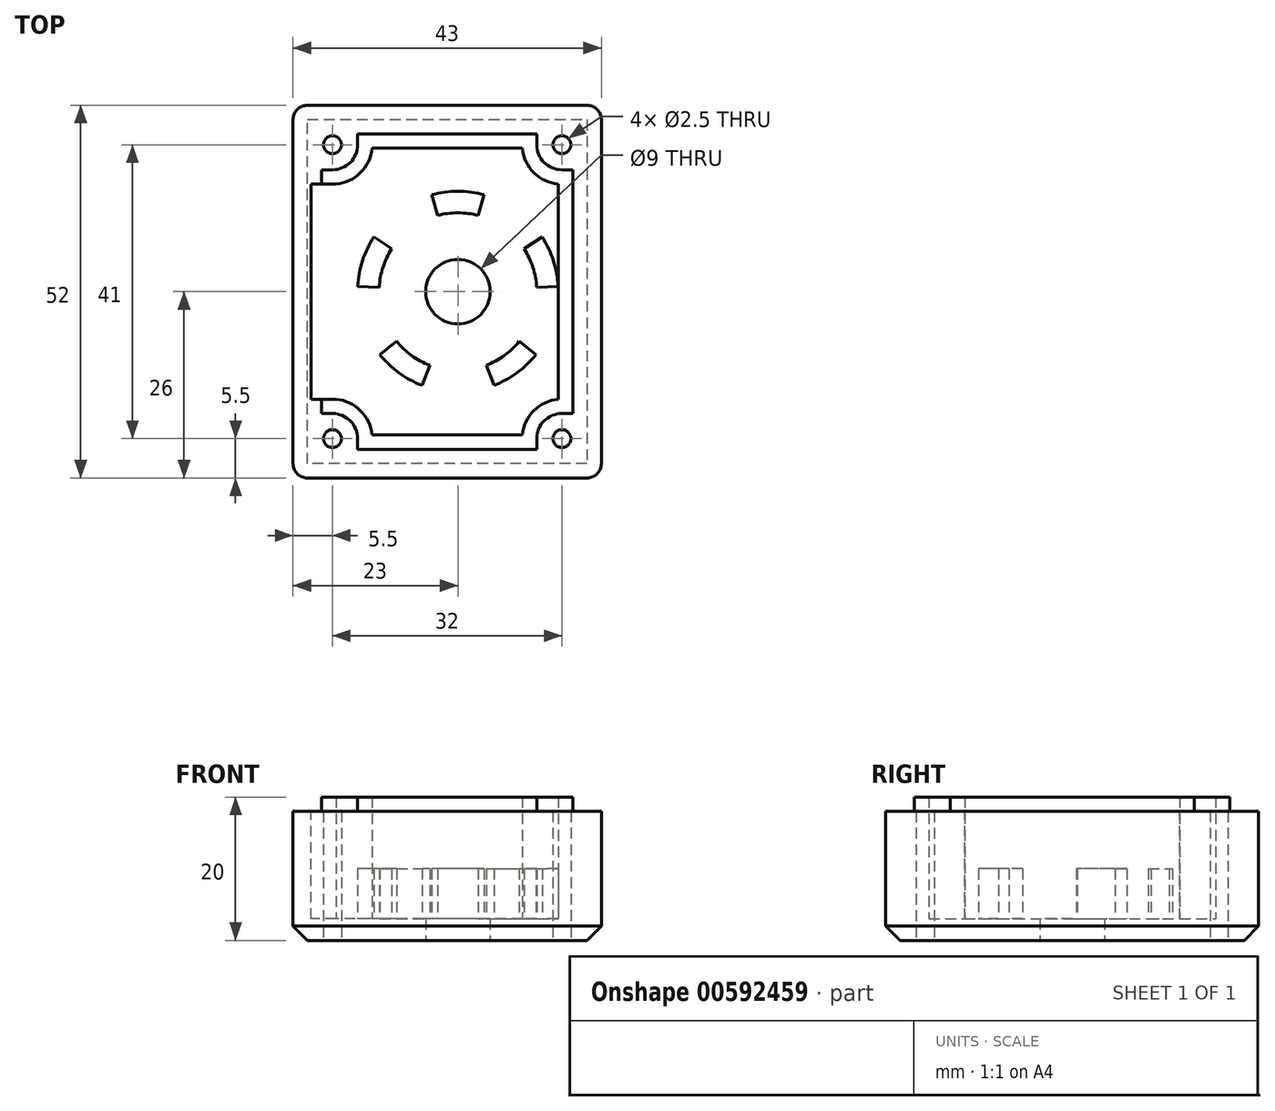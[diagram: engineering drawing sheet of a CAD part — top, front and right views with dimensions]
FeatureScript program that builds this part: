
annotation { "Feature Type Name" : "Feature", "Feature Type Description" : "" }
export const myFeature = defineFeature(function(context is Context, id is Id, definition is map)
    precondition{}
    {
        {
            var Q0;
            Q0=qCreatedBy(makeId("Top.planeOp"),FACE);
            var sketch = newSketch(context, id + "F0", { "sketchPlane" : qUnion([Q0])});
            skLineSegment(sketch, "E0.0", {"start": v(-18.64, 26) * mm, "end": v(20.36, 26) * mm});
            skArc(sketch, "E0.1", {"start": v(-18.64, 26) * mm, "mid": v(-20.05, 25.41) * mm, "end": v(-20.64, 24) * mm});
            skLineSegment(sketch, "E0.2", {"start": v(-20.64, 24) * mm, "end": v(-20.64, -24) * mm});
            skLineSegment(sketch, "E0.3", {"start": v(-17.64, 18) * mm, "end": v(-17.64, -18) * mm});
            skLineSegment(sketch, "E0.4", {"start": v(-15.14, 18) * mm, "end": v(-18.64, 18) * mm});
            skArc(sketch, "E0.5", {"start": v(-15.14, 18) * mm, "mid": v(-13.37, 18.73) * mm, "end": v(-12.64, 20.5) * mm});
            skLineSegment(sketch, "E0.6", {"start": v(-12.64, 20.5) * mm, "end": v(-12.64, 24) * mm});
            skLineSegment(sketch, "E0.7", {"start": v(14.36, 23) * mm, "end": v(-12.64, 23) * mm});
            skLineSegment(sketch, "E0.8", {"start": v(14.36, 20.5) * mm, "end": v(14.36, 24) * mm});
            skArc(sketch, "E0.9", {"start": v(14.36, 20.5) * mm, "mid": v(15.1, 18.73) * mm, "end": v(16.86, 18) * mm});
            skLineSegment(sketch, "E0.10", {"start": v(16.86, 18) * mm, "end": v(20.36, 18) * mm});
            skLineSegment(sketch, "E0.11", {"start": v(19.36, -18) * mm, "end": v(19.36, 18) * mm});
            skLineSegment(sketch, "E0.12", {"start": v(16.86, -18) * mm, "end": v(20.36, -18) * mm});
            skArc(sketch, "E0.13", {"start": v(16.86, -18) * mm, "mid": v(15.1, -18.73) * mm, "end": v(14.36, -20.5) * mm});
            skLineSegment(sketch, "E0.14", {"start": v(14.36, -20.5) * mm, "end": v(14.36, -24) * mm});
            skLineSegment(sketch, "E0.15", {"start": v(-12.64, -23) * mm, "end": v(14.36, -23) * mm});
            skLineSegment(sketch, "E0.16", {"start": v(-12.64, -24) * mm, "end": v(-12.64, -20.5) * mm});
            skArc(sketch, "E0.17", {"start": v(-12.64, -20.5) * mm, "mid": v(-13.37, -18.73) * mm, "end": v(-15.14, -18) * mm});
            skLineSegment(sketch, "E0.18", {"start": v(-15.14, -18) * mm, "end": v(-18.64, -18) * mm});
            skArc(sketch, "E0.20", {"start": v(-20.64, -24) * mm, "mid": v(-20.05, -25.41) * mm, "end": v(-18.64, -26) * mm});
            skLineSegment(sketch, "E0.21", {"start": v(-18.64, -26) * mm, "end": v(20.36, -26) * mm});
            skArc(sketch, "E0.22", {"start": v(20.36, -26) * mm, "mid": v(21.77, -25.41) * mm, "end": v(22.36, -24) * mm});
            skLineSegment(sketch, "E0.23", {"start": v(22.36, 24) * mm, "end": v(22.36, -24) * mm});
            skArc(sketch, "E0.24", {"start": v(22.36, 24) * mm, "mid": v(21.77, 25.41) * mm, "end": v(20.36, 26) * mm});
            skSolve(sketch);
        }
        {
            var Q0;
            Q0=qCreatedBy(makeId("Top.planeOp"),FACE);
            var sketch = newSketch(context, id + "F1", { "sketchPlane" : qUnion([Q0])});
            skLineSegment(sketch, "E1", {"start": v(-16.64, 17) * mm, "end": v(-16.64, -17) * mm});
            skLineSegment(sketch, "E2", {"start": v(-16.64, -17) * mm, "end": v(-15.14, -17) * mm});
            skLineSegment(sketch, "E3", {"start": v(-11.64, -20.5) * mm, "end": v(-11.64, -22) * mm});
            skLineSegment(sketch, "E4", {"start": v(-11.64, -22) * mm, "end": v(13.36, -22) * mm});
            skLineSegment(sketch, "E5", {"start": v(13.36, -22) * mm, "end": v(13.36, -20.5) * mm});
            skLineSegment(sketch, "E6", {"start": v(16.86, -17) * mm, "end": v(18.36, -17) * mm});
            skLineSegment(sketch, "E7", {"start": v(18.36, -17) * mm, "end": v(18.36, 17) * mm});
            skLineSegment(sketch, "E8", {"start": v(18.36, 17) * mm, "end": v(16.86, 17) * mm});
            skLineSegment(sketch, "E9", {"start": v(13.36, 20.5) * mm, "end": v(13.36, 22) * mm});
            skLineSegment(sketch, "E10", {"start": v(13.36, 22) * mm, "end": v(-11.64, 22) * mm});
            skLineSegment(sketch, "E11", {"start": v(-11.64, 22) * mm, "end": v(-11.64, 20.5) * mm});
            skLineSegment(sketch, "E12", {"start": v(-15.14, 17) * mm, "end": v(-16.64, 17) * mm});
            skArc(sketch, "E13", {"start": v(-15.14, 17) * mm, "mid": v(-12.67, 18.03) * mm, "end": v(-11.64, 20.5) * mm});
            skArc(sketch, "E14", {"start": v(13.36, 20.5) * mm, "mid": v(14.39, 18.03) * mm, "end": v(16.86, 17) * mm});
            skArc(sketch, "E15", {"start": v(16.86, -17) * mm, "mid": v(14.39, -18.03) * mm, "end": v(13.36, -20.5) * mm});
            skArc(sketch, "E16", {"start": v(-11.64, -20.5) * mm, "mid": v(-12.67, -18.03) * mm, "end": v(-15.14, -17) * mm});
            skSolve(sketch);
        }
        {
            var Q0;
            Q0=makeQuery(id+"F1.imprint","IMPRINT",FACE,{"disambiguationData":[TD([[makeQuery(id+"F1.imprint","IMPRINT",EDGE,{"derivedFrom":sQuery(id+"F1.wireOp",EDGE,"E1")}),1.0]])]});
            extrude(context, id + "F2", {"entities" : qUnion([Q0]), "depth" : 2 * mm, "offsetDistance" : 25 * mm});
        }
        {
            var Q0;
            Q0=makeQuery(id+"F0.imprint","IMPRINT",FACE,{"disambiguationData":[TD([[makeQuery(id+"F0.imprint","IMPRINT",EDGE,{"derivedFrom":sQuery(id+"F0.wireOp",EDGE,"E0.0")}),-1.0]])]});
            var Q1;
            {var subQ7=sQuery(id+"F0.wireOp",EDGE,"E0.3");Q1=makeQuery(id+"F0.imprint","IMPRINT",FACE,{"disambiguationData":[TD([[makeQuery(id+"F0.imprint","IMPRINT",EDGE,{"derivedFrom":subQ7}),1.0]])]});}
            extrude(context, id + "F3", {"entities" : qUnion([Q0, Q1]), "operationType" : NewBodyOperationType.ADD, "oppositeDirection" : true, "depth" : 3 * mm, "offsetDistance" : 25 * mm});
        }
        {
            var Q0;
            Q0=makeQuery(id+"F3.opExtrude","CAP_FACE",FACE,{"disambiguationData":[OSD([sQuery(id+"F0.wireOp",EDGE,"E0.0"),sQuery(id+"F0.wireOp",EDGE,"E0.1"),sQuery(id+"F0.wireOp",EDGE,"E0.2"),sQuery(id+"F0.wireOp",EDGE,"E0.20"),sQuery(id+"F0.wireOp",EDGE,"E0.21"),sQuery(id+"F0.wireOp",EDGE,"E0.22"),sQuery(id+"F0.wireOp",EDGE,"E0.23"),sQuery(id+"F0.wireOp",EDGE,"E0.24")])],"isStart":false});
            var sketch = newSketch(context, id + "F4", { "sketchPlane" : qUnion([Q0])});
            skCircle(sketch, "E17", {"center": v(2.36, 0) * mm, "radius": 4.5 * mm});
            skPoint(sketch, "E18", {"position": v(22.36, 0) * mm});
            skSolve(sketch);
        }
        {
            var Q0;
            Q0=makeQuery(id+"F4.imprint","IMPRINT",FACE,{"disambiguationData":[TD([[makeQuery(id+"F4.imprint","IMPRINT",EDGE,{"derivedFrom":sQuery(id+"F4.wireOp",EDGE,"E17")}),1.0]])]});
            extrude(context, id + "F5", {"entities" : qUnion([Q0]), "operationType" : NewBodyOperationType.REMOVE, "endBound" : BoundingType.UP_TO_NEXT, "oppositeDirection" : true, "depth" : 25 * mm, "offsetDistance" : 25 * mm});
        }
        {
            var Q0;
            Q0=makeQuery(id+"F3.opExtrude","CAP_FACE",FACE,{"disambiguationData":[OSD([sQuery(id+"F0.wireOp",EDGE,"E0.0"),sQuery(id+"F0.wireOp",EDGE,"E0.1"),sQuery(id+"F0.wireOp",EDGE,"E0.2"),sQuery(id+"F0.wireOp",EDGE,"E0.20"),sQuery(id+"F0.wireOp",EDGE,"E0.21"),sQuery(id+"F0.wireOp",EDGE,"E0.22"),sQuery(id+"F0.wireOp",EDGE,"E0.23"),sQuery(id+"F0.wireOp",EDGE,"E0.24")])],"isStart":false});
            var sketch = newSketch(context, id + "F6", { "sketchPlane" : qUnion([Q0])});
            skPoint(sketch, "E19", {"position": v(16.86, 20.5) * mm});
            skPoint(sketch, "E20", {"position": v(-15.14, -20.5) * mm});
            skPoint(sketch, "E21", {"position": v(-15.14, 20.5) * mm});
            skPoint(sketch, "E22", {"position": v(16.86, -20.5) * mm});
            skSolve(sketch);
        }
        {
            var Q0;
            Q0=sQuery(id+"F6.wireOp",VERTEX,"E21");
            var Q1;
            Q1=sQuery(id+"F6.wireOp",VERTEX,"E19");
            var Q2;
            Q2=sQuery(id+"F6.wireOp",VERTEX,"E22");
            var Q3;
            Q3=sQuery(id+"F6.wireOp",VERTEX,"E20");
            var Q4;
            Q4=makeQuery(id+"F2.opExtrude","SWEPT_BODY",BODY,{"disambiguationData":[OSD([sQuery(id+"F1.wireOp",EDGE,"E1"),sQuery(id+"F1.wireOp",EDGE,"E2"),sQuery(id+"F1.wireOp",EDGE,"E3"),sQuery(id+"F1.wireOp",EDGE,"E4"),sQuery(id+"F1.wireOp",EDGE,"E5"),sQuery(id+"F1.wireOp",EDGE,"E6"),sQuery(id+"F1.wireOp",EDGE,"E7"),sQuery(id+"F1.wireOp",EDGE,"E8"),sQuery(id+"F1.wireOp",EDGE,"E9"),sQuery(id+"F1.wireOp",EDGE,"E10"),sQuery(id+"F1.wireOp",EDGE,"E11"),sQuery(id+"F1.wireOp",EDGE,"E12"),sQuery(id+"F1.wireOp",EDGE,"E13"),sQuery(id+"F1.wireOp",EDGE,"E14"),sQuery(id+"F1.wireOp",EDGE,"E15"),sQuery(id+"F1.wireOp",EDGE,"E16")])]});
            hole(context, id + "F7", {"style" : HoleStyle.SIMPLE, "endStyle" : HoleEndStyle.THROUGH, "standardTappedOrClearance" : lookupTablePath({ "standard" : "ISO", "engagement" : "75%", "pitch" : "0.5 mm", "size" : "M3", "type" : "Tapped" }), "standardBlindInLast" : lookupTablePath({ "standard" : "ISO", "engagement" : "75%", "pitch" : "0.5 mm", "size" : "M3", "type" : "Tapped" }), "holeDiameter" : 2.5 * mm, "majorDiameter" : 3 * mm, "showTappedDepth" : true, "isTappedThrough" : true, "tappedDepth" : 8.5 * mm, "tapClearance" : 3, "startFromSketch" : true, "locations" : qUnion([Q0, Q1, Q2, Q3]), "scope" : qUnion([Q4])});
        }
        {
            var Q0;
            Q0=makeQuery(id+"F2.opExtrude","CAP_FACE",FACE,{"disambiguationData":[OSD([sQuery(id+"F1.wireOp",EDGE,"E1"),sQuery(id+"F1.wireOp",EDGE,"E2"),sQuery(id+"F1.wireOp",EDGE,"E3"),sQuery(id+"F1.wireOp",EDGE,"E4"),sQuery(id+"F1.wireOp",EDGE,"E5"),sQuery(id+"F1.wireOp",EDGE,"E6"),sQuery(id+"F1.wireOp",EDGE,"E7"),sQuery(id+"F1.wireOp",EDGE,"E8"),sQuery(id+"F1.wireOp",EDGE,"E9"),sQuery(id+"F1.wireOp",EDGE,"E10"),sQuery(id+"F1.wireOp",EDGE,"E11"),sQuery(id+"F1.wireOp",EDGE,"E12"),sQuery(id+"F1.wireOp",EDGE,"E13"),sQuery(id+"F1.wireOp",EDGE,"E14"),sQuery(id+"F1.wireOp",EDGE,"E15"),sQuery(id+"F1.wireOp",EDGE,"E16")])],"isStart":false});
            var sketch = newSketch(context, id + "F8", { "sketchPlane" : qUnion([Q0])});
            skLineSegment(sketch, "E23", {"start": v(-9.64, 20) * mm, "end": v(11.36, 20) * mm});
            skLineSegment(sketch, "E24", {"start": v(16.36, 15) * mm, "end": v(16.36, -15) * mm});
            skLineSegment(sketch, "E25", {"start": v(11.36, -20) * mm, "end": v(-9.64, -20) * mm});
            skArc(sketch, "E26", {"start": v(-14.64, 15) * mm, "mid": v(-11.23, 16.6) * mm, "end": v(-9.64, 20) * mm});
            skArc(sketch, "E27", {"start": v(11.36, 20) * mm, "mid": v(12.95, 16.6) * mm, "end": v(16.36, 15) * mm});
            skArc(sketch, "E28", {"start": v(16.36, -15) * mm, "mid": v(12.95, -16.6) * mm, "end": v(11.36, -20) * mm});
            skArc(sketch, "E29", {"start": v(-9.64, -20) * mm, "mid": v(-11.23, -16.6) * mm, "end": v(-14.64, -15) * mm});
            skLineSegment(sketch, "E30", {"start": v(-14.64, 15) * mm, "end": v(-16.64, 15) * mm});
            skLineSegment(sketch, "E31", {"start": v(-14.64, -15) * mm, "end": v(-16.64, -15) * mm});
            skSolve(sketch);
        }
        {
            var Q0;
            Q0=makeQuery(id+"F8.imprint","IMPRINT",FACE,{"disambiguationData":[TD([[makeQuery(id+"F8.imprint","IMPRINT",EDGE,{"derivedFrom":sQuery(id+"F8.wireOp",EDGE,"E23")}),-1.0]])]});
            var Q1;
            Q1=makeQuery(id+"F3.opExtrude","CAP_FACE",FACE,{"disambiguationData":[OSD([sQuery(id+"F0.wireOp",EDGE,"E0.0"),sQuery(id+"F0.wireOp",EDGE,"E0.1"),sQuery(id+"F0.wireOp",EDGE,"E0.2"),sQuery(id+"F0.wireOp",EDGE,"E0.20"),sQuery(id+"F0.wireOp",EDGE,"E0.21"),sQuery(id+"F0.wireOp",EDGE,"E0.22"),sQuery(id+"F0.wireOp",EDGE,"E0.23"),sQuery(id+"F0.wireOp",EDGE,"E0.24")])],"isStart":true});
            extrude(context, id + "F9", {"entities" : qUnion([Q0]), "operationType" : NewBodyOperationType.REMOVE, "endBound" : BoundingType.UP_TO_SURFACE, "oppositeDirection" : true, "depth" : 25 * mm, "endBoundEntityFace" : qUnion([Q1]), "offsetDistance" : 25 * mm});
        }
        {
            var Q0;
            Q0=makeQuery(id+"F3.opExtrude","CAP_FACE",FACE,{"disambiguationData":[OSD([sQuery(id+"F0.wireOp",EDGE,"E0.0"),sQuery(id+"F0.wireOp",EDGE,"E0.1"),sQuery(id+"F0.wireOp",EDGE,"E0.2"),sQuery(id+"F0.wireOp",EDGE,"E0.20"),sQuery(id+"F0.wireOp",EDGE,"E0.21"),sQuery(id+"F0.wireOp",EDGE,"E0.22"),sQuery(id+"F0.wireOp",EDGE,"E0.23"),sQuery(id+"F0.wireOp",EDGE,"E0.24")])],"isStart":false});
            extrude(context, id + "F10", {"entities" : qUnion([Q0]), "operationType" : NewBodyOperationType.ADD, "depth" : 10 * mm, "offsetDistance" : 25 * mm});
        }
        {
            var Q0;
            Q0=makeQuery(id+"F3.opExtrude","CAP_FACE",FACE,{"disambiguationData":[OSD([sQuery(id+"F0.wireOp",EDGE,"E0.0"),sQuery(id+"F0.wireOp",EDGE,"E0.1"),sQuery(id+"F0.wireOp",EDGE,"E0.2"),sQuery(id+"F0.wireOp",EDGE,"E0.20"),sQuery(id+"F0.wireOp",EDGE,"E0.21"),sQuery(id+"F0.wireOp",EDGE,"E0.22"),sQuery(id+"F0.wireOp",EDGE,"E0.23"),sQuery(id+"F0.wireOp",EDGE,"E0.24")])],"isStart":true});
            extrude(context, id + "F11", {"entities" : qUnion([Q0]), "operationType" : NewBodyOperationType.ADD, "depth" : 5 * mm, "offsetDistance" : 25 * mm});
        }
        {
            var Q0;
            Q0=makeQuery(id+"F2.opExtrude","CAP_FACE",FACE,{"disambiguationData":[OSD([sQuery(id+"F1.wireOp",EDGE,"E1"),sQuery(id+"F1.wireOp",EDGE,"E2"),sQuery(id+"F1.wireOp",EDGE,"E3"),sQuery(id+"F1.wireOp",EDGE,"E4"),sQuery(id+"F1.wireOp",EDGE,"E5"),sQuery(id+"F1.wireOp",EDGE,"E6"),sQuery(id+"F1.wireOp",EDGE,"E7"),sQuery(id+"F1.wireOp",EDGE,"E8"),sQuery(id+"F1.wireOp",EDGE,"E9"),sQuery(id+"F1.wireOp",EDGE,"E10"),sQuery(id+"F1.wireOp",EDGE,"E11"),sQuery(id+"F1.wireOp",EDGE,"E12"),sQuery(id+"F1.wireOp",EDGE,"E13"),sQuery(id+"F1.wireOp",EDGE,"E14"),sQuery(id+"F1.wireOp",EDGE,"E15"),sQuery(id+"F1.wireOp",EDGE,"E16")])],"isStart":false});
            extrude(context, id + "F12", {"entities" : qUnion([Q0]), "operationType" : NewBodyOperationType.ADD, "depth" : 5 * mm, "offsetDistance" : 25 * mm});
        }
        {
            var Q0;
            Q0=makeQuery(id+"F11.opExtrude","CAP_FACE",FACE,{"disambiguationData":[OSD([sQuery(id+"F0.wireOp",EDGE,"E0.0"),sQuery(id+"F0.wireOp",EDGE,"E0.1"),sQuery(id+"F0.wireOp",EDGE,"E0.2"),sQuery(id+"F0.wireOp",EDGE,"E0.20"),sQuery(id+"F0.wireOp",EDGE,"E0.21"),sQuery(id+"F0.wireOp",EDGE,"E0.22"),sQuery(id+"F0.wireOp",EDGE,"E0.23"),sQuery(id+"F0.wireOp",EDGE,"E0.24")])],"isStart":false});
            var sketch = newSketch(context, id + "F13", { "sketchPlane" : qUnion([Q0])});
            skLineSegment(sketch, "E32", {"start": v(-16.64, -15) * mm, "end": v(-18.14, -15) * mm});
            skLineSegment(sketch, "E33", {"start": v(-18.14, -15) * mm, "end": v(-18.14, 15) * mm});
            skLineSegment(sketch, "E34", {"start": v(-18.14, 15) * mm, "end": v(-16.64, 15) * mm});
            skSolve(sketch);
        }
        {
            var Q0;
            Q0=makeQuery(id+"F13.imprint","IMPRINT",FACE,{"disambiguationData":[TD([[makeQuery(id+"F13.imprint","IMPRINT",EDGE,{"derivedFrom":sQuery(id+"F13.wireOp",EDGE,"E32")}),-1.0]])]});
            extrude(context, id + "F14", {"entities" : qUnion([Q0]), "operationType" : NewBodyOperationType.REMOVE, "oppositeDirection" : true, "depth" : 15 * mm, "offsetDistance" : 25 * mm});
        }
        {
            var Q0;
            Q0=makeQuery(id+"F14.boolean.opBoolean","COPY",FACE,{"derivedFrom":makeQuery(id+"F14.opExtrude","CAP_FACE",FACE,{"disambiguationData":[OSD([sQuery(id+"F0.wireOp",EDGE,"E0.0"),sQuery(id+"F0.wireOp",EDGE,"E0.1"),sQuery(id+"F0.wireOp",EDGE,"E0.2"),sQuery(id+"F0.wireOp",EDGE,"E0.20"),sQuery(id+"F0.wireOp",EDGE,"E0.21"),sQuery(id+"F0.wireOp",EDGE,"E0.22"),sQuery(id+"F0.wireOp",EDGE,"E0.23"),sQuery(id+"F0.wireOp",EDGE,"E0.24"),sQuery(id+"F1.wireOp",EDGE,"E1"),sQuery(id+"F1.wireOp",EDGE,"E2"),sQuery(id+"F1.wireOp",EDGE,"E3"),sQuery(id+"F1.wireOp",EDGE,"E4"),sQuery(id+"F1.wireOp",EDGE,"E5"),sQuery(id+"F1.wireOp",EDGE,"E6"),sQuery(id+"F1.wireOp",EDGE,"E7"),sQuery(id+"F1.wireOp",EDGE,"E8"),sQuery(id+"F1.wireOp",EDGE,"E9"),sQuery(id+"F1.wireOp",EDGE,"E10"),sQuery(id+"F1.wireOp",EDGE,"E11"),sQuery(id+"F1.wireOp",EDGE,"E12"),sQuery(id+"F1.wireOp",EDGE,"E13"),sQuery(id+"F1.wireOp",EDGE,"E14"),sQuery(id+"F1.wireOp",EDGE,"E15"),sQuery(id+"F1.wireOp",EDGE,"E16"),sQuery(id+"F4.wireOp",EDGE,"E17"),sQuery(id+"F8.wireOp",EDGE,"E23"),sQuery(id+"F8.wireOp",EDGE,"E24"),sQuery(id+"F8.wireOp",EDGE,"E25"),sQuery(id+"F8.wireOp",EDGE,"E26"),sQuery(id+"F8.wireOp",EDGE,"E27"),sQuery(id+"F8.wireOp",EDGE,"E28"),sQuery(id+"F8.wireOp",EDGE,"E29"),sQuery(id+"F8.wireOp",EDGE,"E30"),sQuery(id+"F8.wireOp",EDGE,"E31"),sQuery(id+"F13.wireOp",EDGE,"E32"),sQuery(id+"F13.wireOp",EDGE,"E33"),sQuery(id+"F13.wireOp",EDGE,"E34")])],"isStart":false})});
            var sketch = newSketch(context, id + "F15", { "sketchPlane" : qUnion([Q0])});
            skCircle(sketch, "E35", {"center": v(2.36, 0) * mm, "radius": 11 * mm});
            skCircle(sketch, "E36", {"center": v(2.36, 0) * mm, "radius": 14 * mm});
            skLineSegment(sketch, "E37", {"start": v(2.36, 0) * mm, "end": v(-1.26, 13.52) * mm});
            skLineSegment(sketch, "E38", {"start": v(2.36, 0) * mm, "end": v(5.98, 13.52) * mm});
            skSolve(sketch);
        }
        {
            var Q0;
            {var subQ0=sQuery(id+"F15.wireOp",EDGE,"E37");var subQ1=sQuery(id+"F15.wireOp",EDGE,"E35");var subQ2=makeQuery(id+"F15.imprint","INTERSECT",VERTEX,{"derivedFrom":[subQ1,subQ0]});Q0=makeQuery(id+"F15.imprint","IMPRINT",FACE,{"disambiguationData":[TD([[makeQuery(id+"F15.imprint","IMPRINT",EDGE,{"disambiguationData":[TD([[subQ2,1.0]])],"derivedFrom":subQ1}),-1.0]])]});}
            extrude(context, id + "F16", {"entities" : qUnion([Q0]), "depth" : 7 * mm, "offsetDistance" : 25 * mm});
        }
        {
            var Q0;
            Q0=qCreatedBy(makeId("Front.planeOp"),FACE);
            var sketch = newSketch(context, id + "F17", { "sketchPlane" : qUnion([Q0])});
            skLineSegment(sketch, "E39", {"start": v(2.36, -10) * mm, "end": v(2.36, 31.24) * mm});
            skSolve(sketch);
        }
        {
            var Q0;
            Q0=makeQuery(id+"F16.opExtrude","SWEPT_BODY",BODY,{"disambiguationData":[OSD([sQuery(id+"F15.wireOp",EDGE,"E35"),sQuery(id+"F15.wireOp",EDGE,"E36"),sQuery(id+"F15.wireOp",EDGE,"E37"),sQuery(id+"F15.wireOp",EDGE,"E38")])]});
            var Q1;
            Q1=sQuery(id+"F17.wireOp",EDGE,"E39");
            circularPattern(context, id + "F18", {"operationType" : NewBodyOperationType.ADD, "entities" : qUnion([Q0]), "axis" : qUnion([Q1]), "angle" : 360 * degree, "instanceCount" : 5, "equalSpace" : true});
        }
        {
            var Q0;
            Q0=makeQuery(id+"F10.opExtrude","CAP_EDGE",EDGE,{"disambiguationData":[OSD([sQuery(id+"F0.wireOp",EDGE,"E0.21")])],"isStart":false});
            var Q1;
            Q1=makeQuery(id+"F10.opExtrude","CAP_EDGE",EDGE,{"disambiguationData":[OSD([sQuery(id+"F0.wireOp",EDGE,"E0.2")])],"isStart":false});
            var Q2;
            Q2=makeQuery(id+"F10.opExtrude","CAP_EDGE",EDGE,{"disambiguationData":[OSD([sQuery(id+"F0.wireOp",EDGE,"E0.0")])],"isStart":false});
            chamfer(context, id + "F19", {"entities" : qUnion([Q0, Q1, Q2]), "width" : 2 * mm, "tangentPropagation" : true});
        }
    });
